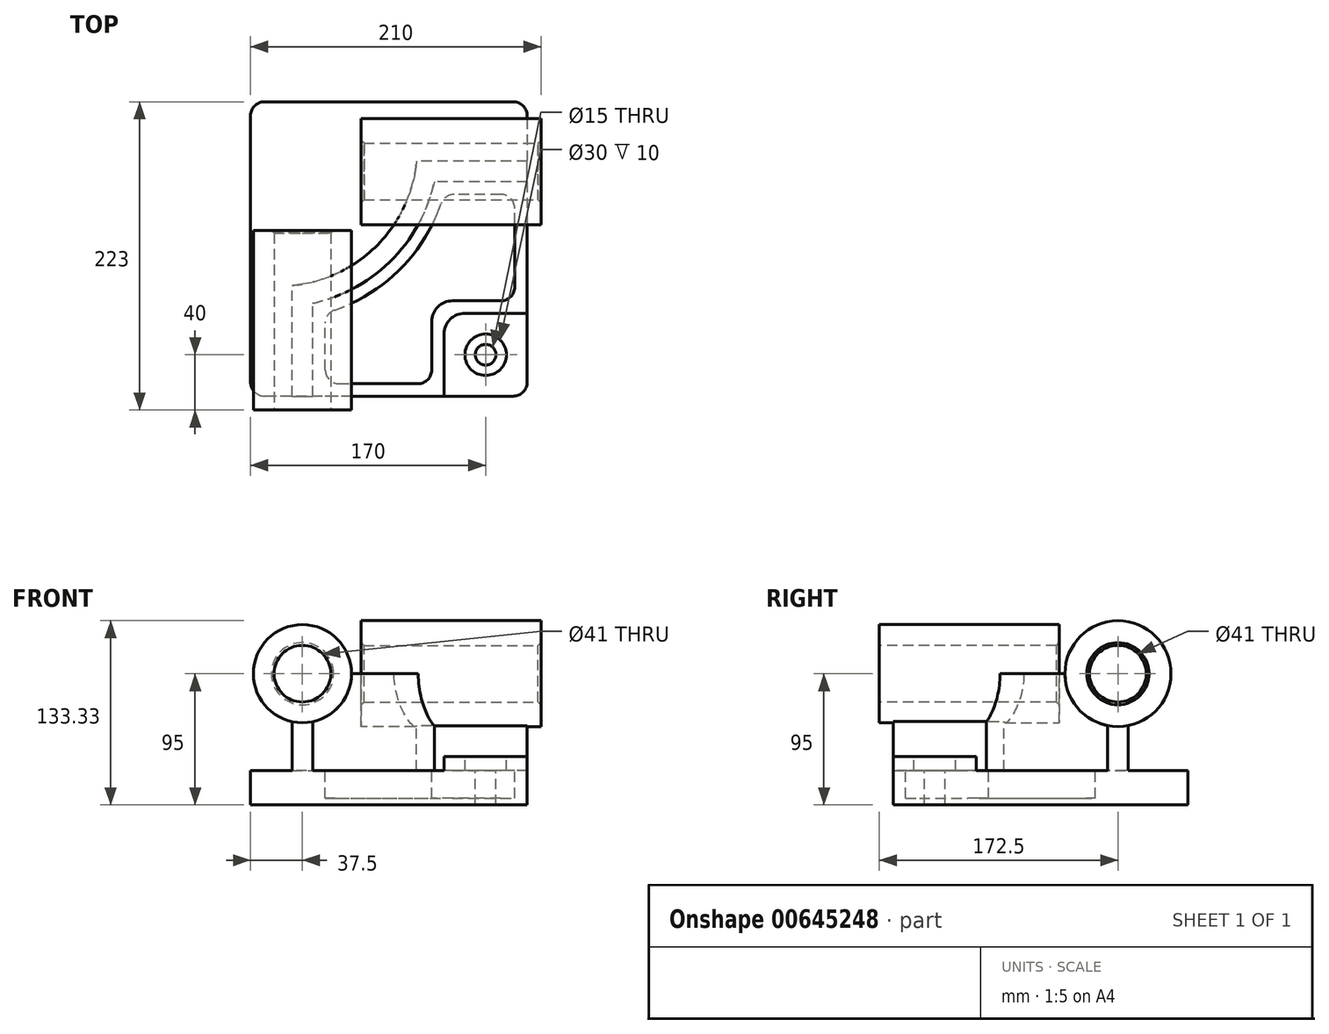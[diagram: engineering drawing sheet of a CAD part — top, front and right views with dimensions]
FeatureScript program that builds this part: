
annotation { "Feature Type Name" : "Feature", "Feature Type Description" : "" }
export const myFeature = defineFeature(function(context is Context, id is Id, definition is map)
    precondition{}
    {
        {
            var Q0;
            Q0=qCreatedBy(makeId("Top.planeOp"),FACE);
            var sketch = newSketch(context, id + "F0", { "sketchPlane" : qUnion([Q0])});
            skLineSegment(sketch, "E0.bottom", {"start": v(100, 106.5) * mm, "end": v(-100, 106.5) * mm});
            skLineSegment(sketch, "E0.top", {"start": v(100, -106.5) * mm, "end": v(-100, -106.5) * mm});
            skLineSegment(sketch, "E0.left", {"start": v(100, 106.5) * mm, "end": v(100, -106.5) * mm});
            skLineSegment(sketch, "E0.right", {"start": v(-100, 106.5) * mm, "end": v(-100, -106.5) * mm});
            skPoint(sketch, "E0.middle", {"position": v(0, 0) * mm});
            skSolve(sketch);
        }
        {
            var Q0;
            Q0 = qSketchRegion(id + "F0", true);
            var Q1;
            Q1=makeQuery(id+"F0.imprint","IMPRINT",FACE,{"disambiguationData":[TD([[makeQuery(id+"F0.imprint","IMPRINT",EDGE,{"derivedFrom":sQuery(id+"F0.wireOp",EDGE,"E0.bottom")}),1.0]])]});
            extrude(context, id + "F1", {"entities" : qUnion([Q0, Q1]), "depth" : 95 * mm, "offsetDistance" : 25 * mm});
        }
        {
            var Q0;
            Q0=makeQuery(id+"F1.opExtrude","CAP_FACE",FACE,{"disambiguationData":[OSD([sQuery(id+"F0.wireOp",EDGE,"E0.bottom"),sQuery(id+"F0.wireOp",EDGE,"E0.top"),sQuery(id+"F0.wireOp",EDGE,"E0.left"),sQuery(id+"F0.wireOp",EDGE,"E0.right")])],"isStart":false});
            var sketch = newSketch(context, id + "F2", { "sketchPlane" : qUnion([Q0])});
            skLineSegment(sketch, "E1", {"start": v(-70, -106.5) * mm, "end": v(-70, -26.5) * mm});
            skLineSegment(sketch, "E2", {"start": v(100, 63.5) * mm, "end": v(20, 63.5) * mm});
            skLineSegment(sketch, "E3.bottom", {"start": v(100, -106.5) * mm, "end": v(40, -106.5) * mm});
            skLineSegment(sketch, "E3.top", {"start": v(100, -46.5) * mm, "end": v(40, -46.5) * mm});
            skLineSegment(sketch, "E3.left", {"start": v(100, -106.5) * mm, "end": v(100, -46.5) * mm});
            skLineSegment(sketch, "E3.right", {"start": v(40, -106.5) * mm, "end": v(40, -46.5) * mm});
            skPoint(sketch, "E4.positionSnap0", {"position": v(70, -106.5) * mm});
            skLineSegment(sketch, "E5", {"start": v(70, -46.5) * mm, "end": v(70, -106.5) * mm, "construction": true});
            skPoint(sketch, "E6", {"position": v(70, -76.5) * mm});
            skArc(sketch, "E7", {"start": v(-70, -26.5) * mm, "mid": v(-8.83, 2.33) * mm, "end": v(20, 63.5) * mm});
            skLineSegment(sketch, "E8.0", {"start": v(-55, -106.5) * mm, "end": v(-55, -39.3) * mm});
            skArc(sketch, "E8.1", {"start": v(-55, -39.3) * mm, "mid": v(1.77, -8.27) * mm, "end": v(32.8, 48.5) * mm});
            skLineSegment(sketch, "E8.2", {"start": v(100, 48.5) * mm, "end": v(32.8, 48.5) * mm});
            skLineSegment(sketch, "E9.0", {"start": v(-46, -97.5) * mm, "end": v(-46, -46.33) * mm});
            skArc(sketch, "E9.1", {"start": v(-46, -46.33) * mm, "mid": v(8.14, -14.64) * mm, "end": v(39.83, 39.5) * mm});
            skLineSegment(sketch, "E9.2", {"start": v(91, 39.5) * mm, "end": v(39.83, 39.5) * mm});
            skLineSegment(sketch, "E10", {"start": v(-46, -97.5) * mm, "end": v(31, -97.5) * mm});
            skLineSegment(sketch, "E11", {"start": v(31, -97.5) * mm, "end": v(31, -37.5) * mm});
            skLineSegment(sketch, "E12", {"start": v(31, -37.5) * mm, "end": v(91, -37.5) * mm});
            skLineSegment(sketch, "E13", {"start": v(91, -37.5) * mm, "end": v(91, 39.5) * mm});
            skSolve(sketch);
        }
        {
            var Q0;
            Q0=makeQuery(id+"F2.imprint","IMPRINT",FACE,{"disambiguationData":[TD([[makeQuery(id+"F2.imprint","IMPRINT",EDGE,{"derivedFrom":sQuery(id+"F2.wireOp",EDGE,"E3.bottom")}),-1.0]])]});
            extrude(context, id + "F3", {"entities" : qUnion([Q0]), "operationType" : NewBodyOperationType.REMOVE, "oppositeDirection" : true, "depth" : 60 * mm, "offsetDistance" : 25 * mm});
        }
        {
            var Q0;
            Q0=makeQuery(id+"F2.imprint","IMPRINT",FACE,{"disambiguationData":[TD([[makeQuery(id+"F2.imprint","IMPRINT",EDGE,{"derivedFrom":sQuery(id+"F2.wireOp",EDGE,"E9.0")}),-1.0]])]});
            extrude(context, id + "F4", {"entities" : qUnion([Q0]), "operationType" : NewBodyOperationType.REMOVE, "oppositeDirection" : true, "depth" : 90 * mm, "offsetDistance" : 25 * mm});
        }
        {
            var Q0;
            {var subQ1=sQuery(id+"F2.wireOp",EDGE,"E3.top");Q0=makeQuery(id+"F2.imprint","IMPRINT",FACE,{"disambiguationData":[TD([[makeQuery(id+"F2.imprint","IMPRINT",EDGE,{"derivedFrom":subQ1}),-1.0]])]});}
            extrude(context, id + "F5", {"entities" : qUnion([Q0]), "operationType" : NewBodyOperationType.REMOVE, "oppositeDirection" : true, "depth" : 70 * mm, "offsetDistance" : 25 * mm});
        }
        {
            var Q0;
            {var subQ2=sQuery(id+"F2.wireOp",EDGE,"E1");Q0=makeQuery(id+"F2.imprint","IMPRINT",FACE,{"disambiguationData":[TD([[makeQuery(id+"F2.imprint","IMPRINT",EDGE,{"derivedFrom":subQ2}),1.0]])]});}
            extrude(context, id + "F6", {"entities" : qUnion([Q0]), "operationType" : NewBodyOperationType.REMOVE, "oppositeDirection" : true, "depth" : 70 * mm, "offsetDistance" : 25 * mm});
        }
        {
            var Q0;
            Q0=makeQuery(id+"F1.opExtrude","SWEPT_FACE",FACE,{"disambiguationData":[OSD([sQuery(id+"F0.wireOp",EDGE,"E0.top")])]});
            var sketch = newSketch(context, id + "F7", { "sketchPlane" : qUnion([Q0])});
            skPoint(sketch, "E14", {"position": v(-62.5, 95) * mm});
            skCircle(sketch, "E15", {"center": v(-62.5, 95) * mm, "radius": 35.5 * mm});
            skCircle(sketch, "E16", {"center": v(-62.5, 95) * mm, "radius": 20.5 * mm});
            skSolve(sketch);
        }
        {
            var Q0;
            Q0=makeQuery(id+"F1.opExtrude","SWEPT_FACE",FACE,{"disambiguationData":[OSD([sQuery(id+"F0.wireOp",EDGE,"E0.left")])]});
            var sketch = newSketch(context, id + "F8", { "sketchPlane" : qUnion([Q0])});
            skPoint(sketch, "E17", {"position": v(56, 95) * mm});
            skCircle(sketch, "E18", {"center": v(56, 95) * mm, "radius": 38.33 * mm});
            skCircle(sketch, "E19", {"center": v(56, 95) * mm, "radius": 20.5 * mm});
            skSolve(sketch);
        }
        {
            var Q0;
            {var subQ1=sQuery(id+"F0.wireOp",EDGE,"E0.top");var subQ6=makeQuery(id+"F1.opExtrude","CAP_EDGE",EDGE,{"disambiguationData":[OSD([subQ1])],"isStart":false});Q0=makeQuery(id+"F7.imprint","IMPRINT",FACE,{"disambiguationData":[TD([[makeQuery(id+"F7.imprint","IMPRINT",EDGE,{"derivedFrom":subQ6}),-1.0]])]});}
            var Q1;
            {var subQ1=sQuery(id+"F0.wireOp",EDGE,"E0.top");var subQ6=makeQuery(id+"F1.opExtrude","CAP_EDGE",EDGE,{"disambiguationData":[OSD([subQ1])],"isStart":false});Q1=makeQuery(id+"F7.imprint","IMPRINT",FACE,{"disambiguationData":[TD([[makeQuery(id+"F7.imprint","IMPRINT",EDGE,{"derivedFrom":subQ6}),1.0]])]});}
            var Q2;
            {var subQ0=sQuery(id+"F7.wireOp",EDGE,"E15");var subQ1=sQuery(id+"F0.wireOp",EDGE,"E0.top");var subQ2=makeQuery(id+"F5.boolean.opBoolean","COPY",EDGE,{"derivedFrom":makeQuery(id+"F5.opExtrude","SWEPT_EDGE",EDGE,{"disambiguationData":[OSD([subQ1,sQuery(id+"F2.wireOp",EDGE,"E8.0")])]})});var subQ3=makeQuery(id+"F7.imprint","INTERSECT",VERTEX,{"derivedFrom":[subQ2,subQ0]});Q2=makeQuery(id+"F7.imprint","IMPRINT",FACE,{"disambiguationData":[TD([[makeQuery(id+"F7.imprint","IMPRINT",EDGE,{"disambiguationData":[TD([[subQ3,-1.0]])],"derivedFrom":subQ0}),1.0]])]});}
            var Q3;
            {var subQ0=sQuery(id+"F7.wireOp",EDGE,"E15");var subQ1=sQuery(id+"F0.wireOp",EDGE,"E0.top");var subQ2=makeQuery(id+"F5.boolean.opBoolean","COPY",EDGE,{"derivedFrom":makeQuery(id+"F5.opExtrude","SWEPT_EDGE",EDGE,{"disambiguationData":[OSD([subQ1,sQuery(id+"F2.wireOp",EDGE,"E8.0")])]})});var subQ3=makeQuery(id+"F7.imprint","INTERSECT",VERTEX,{"derivedFrom":[subQ2,subQ0]});Q3=makeQuery(id+"F7.imprint","IMPRINT",FACE,{"disambiguationData":[TD([[makeQuery(id+"F7.imprint","IMPRINT",EDGE,{"disambiguationData":[TD([[subQ3,1.0]])],"derivedFrom":subQ0}),1.0]])]});}
            extrude(context, id + "F9", {"entities" : qUnion([Q0, Q1, Q2, Q3]), "operationType" : NewBodyOperationType.ADD, "depth" : 10 * mm, "offsetDistance" : 25 * mm, "hasSecondDirection" : true, "secondDirectionOppositeDirection" : true, "secondDirectionDepth" : 120 * mm});
        }
        {
            var Q0;
            Q0=makeQuery(id+"F9.opExtrude","CAP_FACE",FACE,{"disambiguationData":[OSD([sQuery(id+"F7.wireOp",EDGE,"E15")])],"isStart":false});
            var sketch = newSketch(context, id + "F10", { "sketchPlane" : qUnion([Q0])});
            skCircle(sketch, "E20", {"center": v(-62.5, 95) * mm, "radius": 20.5 * mm});
            skSolve(sketch);
        }
        {
            var Q0;
            Q0=makeQuery(id+"F10.imprint","IMPRINT",FACE,{"disambiguationData":[TD([[makeQuery(id+"F10.imprint","IMPRINT",EDGE,{"derivedFrom":sQuery(id+"F10.wireOp",EDGE,"E20")}),1.0]])]});
            extrude(context, id + "F11", {"entities" : qUnion([Q0]), "operationType" : NewBodyOperationType.REMOVE, "endBound" : BoundingType.THROUGH_ALL, "oppositeDirection" : true, "depth" : 25 * mm, "offsetDistance" : 25 * mm});
        }
        {
            var Q0;
            {var subQ1=sQuery(id+"F0.wireOp",EDGE,"E0.left");var subQ6=makeQuery(id+"F1.opExtrude","CAP_EDGE",EDGE,{"disambiguationData":[OSD([subQ1])],"isStart":false});Q0=makeQuery(id+"F8.imprint","IMPRINT",FACE,{"disambiguationData":[TD([[makeQuery(id+"F8.imprint","IMPRINT",EDGE,{"derivedFrom":subQ6}),-1.0]])]});}
            var Q1;
            {var subQ0=sQuery(id+"F8.wireOp",EDGE,"E18");var subQ1=sQuery(id+"F0.wireOp",EDGE,"E0.left");var subQ2=makeQuery(id+"F5.boolean.opBoolean","COPY",EDGE,{"derivedFrom":makeQuery(id+"F5.opExtrude","SWEPT_EDGE",EDGE,{"disambiguationData":[OSD([subQ1,sQuery(id+"F2.wireOp",EDGE,"E8.2")])]})});var subQ3=makeQuery(id+"F8.imprint","INTERSECT",VERTEX,{"derivedFrom":[subQ2,subQ0]});Q1=makeQuery(id+"F8.imprint","IMPRINT",FACE,{"disambiguationData":[TD([[makeQuery(id+"F8.imprint","IMPRINT",EDGE,{"disambiguationData":[TD([[subQ3,1.0]])],"derivedFrom":subQ0}),1.0]])]});}
            var Q2;
            {var subQ1=sQuery(id+"F0.wireOp",EDGE,"E0.left");var subQ6=makeQuery(id+"F1.opExtrude","CAP_EDGE",EDGE,{"disambiguationData":[OSD([subQ1])],"isStart":false});Q2=makeQuery(id+"F8.imprint","IMPRINT",FACE,{"disambiguationData":[TD([[makeQuery(id+"F8.imprint","IMPRINT",EDGE,{"derivedFrom":subQ6}),1.0]])]});}
            var Q3;
            {var subQ0=sQuery(id+"F8.wireOp",EDGE,"E18");var subQ1=sQuery(id+"F0.wireOp",EDGE,"E0.left");var subQ2=makeQuery(id+"F5.boolean.opBoolean","COPY",EDGE,{"derivedFrom":makeQuery(id+"F5.opExtrude","SWEPT_EDGE",EDGE,{"disambiguationData":[OSD([subQ1,sQuery(id+"F2.wireOp",EDGE,"E8.2")])]})});var subQ3=makeQuery(id+"F8.imprint","INTERSECT",VERTEX,{"derivedFrom":[subQ2,subQ0]});Q3=makeQuery(id+"F8.imprint","IMPRINT",FACE,{"disambiguationData":[TD([[makeQuery(id+"F8.imprint","IMPRINT",EDGE,{"disambiguationData":[TD([[subQ3,-1.0]])],"derivedFrom":subQ0}),1.0]])]});}
            extrude(context, id + "F12", {"entities" : qUnion([Q0, Q1, Q2, Q3]), "operationType" : NewBodyOperationType.ADD, "depth" : 10 * mm, "offsetDistance" : 25 * mm, "hasSecondDirection" : true, "secondDirectionOppositeDirection" : true, "secondDirectionDepth" : 120 * mm});
        }
        {
            var Q0;
            {var subQ1=sQuery(id+"F0.wireOp",EDGE,"E0.left");var subQ6=makeQuery(id+"F1.opExtrude","CAP_EDGE",EDGE,{"disambiguationData":[OSD([subQ1])],"isStart":false});Q0=makeQuery(id+"F8.imprint","IMPRINT",FACE,{"disambiguationData":[TD([[makeQuery(id+"F8.imprint","IMPRINT",EDGE,{"derivedFrom":subQ6}),-1.0]])]});}
            var Q1;
            {var subQ1=sQuery(id+"F0.wireOp",EDGE,"E0.left");var subQ6=makeQuery(id+"F1.opExtrude","CAP_EDGE",EDGE,{"disambiguationData":[OSD([subQ1])],"isStart":false});Q1=makeQuery(id+"F8.imprint","IMPRINT",FACE,{"disambiguationData":[TD([[makeQuery(id+"F8.imprint","IMPRINT",EDGE,{"derivedFrom":subQ6}),1.0]])]});}
            extrude(context, id + "F13", {"entities" : qUnion([Q0, Q1]), "operationType" : NewBodyOperationType.REMOVE, "endBound" : BoundingType.THROUGH_ALL, "oppositeDirection" : true, "depth" : 25 * mm, "offsetDistance" : 25 * mm, "hasSecondDirection" : true, "secondDirectionBound" : SecondDirectionBoundingType.THROUGH_ALL, "secondDirectionOppositeDirection" : false, "secondDirectionDepth" : 25 * mm});
        }
        {
            var Q0;
            Q0=makeQuery(id+"F3.boolean.opBoolean","COPY",FACE,{"derivedFrom":makeQuery(id+"F3.opExtrude","CAP_FACE",FACE,{"disambiguationData":[OSD([sQuery(id+"F2.wireOp",EDGE,"E3.bottom"),sQuery(id+"F2.wireOp",EDGE,"E3.top"),sQuery(id+"F2.wireOp",EDGE,"E3.left"),sQuery(id+"F2.wireOp",EDGE,"E3.right")])],"isStart":false})});
            var sketch = newSketch(context, id + "F14", { "sketchPlane" : qUnion([Q0])});
            skPoint(sketch, "E21", {"position": v(70, -76.5) * mm});
            skPoint(sketch, "E21.positionSnap0", {"position": v(70, -46.5) * mm});
            skSolve(sketch);
        }
        {
            var Q0;
            Q0=sQuery(id+"F14.wireOp",VERTEX,"E21");
            var Q1;
            Q1=makeQuery(id+"F1.opExtrude","SWEPT_BODY",BODY,{"disambiguationData":[OSD([sQuery(id+"F0.wireOp",EDGE,"E0.bottom"),sQuery(id+"F0.wireOp",EDGE,"E0.top"),sQuery(id+"F0.wireOp",EDGE,"E0.left"),sQuery(id+"F0.wireOp",EDGE,"E0.right")])]});
            hole(context, id + "F15", {"style" : HoleStyle.C_BORE, "endStyle" : HoleEndStyle.THROUGH, "holeDiameter" : 15 * mm, "cBoreDiameter" : 30 * mm, "cBoreDepth" : 10 * mm, "majorDiameter" : 6.35 * mm, "isTappedThrough" : true, "tappedDepth" : 12 * mm, "tapClearance" : 3, "startFromSketch" : true, "locations" : qUnion([Q0]), "scope" : qUnion([Q1])});
        }
        {
            var Q0;
            Q0=makeQuery(id+"F1.opExtrude","SWEPT_EDGE",EDGE,{"disambiguationData":[OSD([sQuery(id+"F0.wireOp",EDGE,"E0.bottom"),sQuery(id+"F0.wireOp",EDGE,"E0.right")])]});
            var Q1;
            Q1=makeQuery(id+"F1.opExtrude","SWEPT_EDGE",EDGE,{"disambiguationData":[OSD([sQuery(id+"F0.wireOp",EDGE,"E0.bottom"),sQuery(id+"F0.wireOp",EDGE,"E0.left")])]});
            var Q2;
            Q2=makeQuery(id+"F1.opExtrude","SWEPT_EDGE",EDGE,{"disambiguationData":[OSD([sQuery(id+"F0.wireOp",EDGE,"E0.top"),sQuery(id+"F0.wireOp",EDGE,"E0.left")])]});
            var Q3;
            Q3=makeQuery(id+"F1.opExtrude","SWEPT_EDGE",EDGE,{"disambiguationData":[OSD([sQuery(id+"F0.wireOp",EDGE,"E0.top"),sQuery(id+"F0.wireOp",EDGE,"E0.right")])]});
            fillet(context, id + "F16", {"entities" : qUnion([Q0, Q1, Q2, Q3]), "radius" : 10 * mm, "tangentPropagation" : true, "allowEdgeOverflow" : false});
        }
        {
            var Q0;
            Q0=makeQuery(id+"F4.boolean.opBoolean","COPY",EDGE,{"derivedFrom":makeQuery(id+"F4.opExtrude","SWEPT_EDGE",EDGE,{"disambiguationData":[OSD([sQuery(id+"F2.wireOp",EDGE,"E9.1"),sQuery(id+"F2.wireOp",EDGE,"E9.2")])]})});
            var Q1;
            Q1=makeQuery(id+"F4.boolean.opBoolean","COPY",EDGE,{"derivedFrom":makeQuery(id+"F4.opExtrude","SWEPT_EDGE",EDGE,{"disambiguationData":[OSD([sQuery(id+"F2.wireOp",EDGE,"E9.2"),sQuery(id+"F2.wireOp",EDGE,"E13")])]})});
            var Q2;
            Q2=makeQuery(id+"F4.boolean.opBoolean","COPY",EDGE,{"derivedFrom":makeQuery(id+"F4.opExtrude","SWEPT_EDGE",EDGE,{"disambiguationData":[OSD([sQuery(id+"F2.wireOp",EDGE,"E12"),sQuery(id+"F2.wireOp",EDGE,"E13")])]})});
            var Q3;
            Q3=makeQuery(id+"F4.boolean.opBoolean","COPY",EDGE,{"derivedFrom":makeQuery(id+"F4.opExtrude","SWEPT_EDGE",EDGE,{"disambiguationData":[OSD([sQuery(id+"F2.wireOp",EDGE,"E9.0"),sQuery(id+"F2.wireOp",EDGE,"E9.1")])]})});
            var Q4;
            Q4=makeQuery(id+"F4.boolean.opBoolean","COPY",EDGE,{"derivedFrom":makeQuery(id+"F4.opExtrude","SWEPT_EDGE",EDGE,{"disambiguationData":[OSD([sQuery(id+"F2.wireOp",EDGE,"E9.0"),sQuery(id+"F2.wireOp",EDGE,"E10")])]})});
            var Q5;
            Q5=makeQuery(id+"F4.boolean.opBoolean","COPY",EDGE,{"derivedFrom":makeQuery(id+"F4.opExtrude","SWEPT_EDGE",EDGE,{"disambiguationData":[OSD([sQuery(id+"F2.wireOp",EDGE,"E10"),sQuery(id+"F2.wireOp",EDGE,"E11")])]})});
            fillet(context, id + "F17", {"entities" : qUnion([Q0, Q1, Q2, Q3, Q4, Q5]), "radius" : 10 * mm, "tangentPropagation" : true, "allowEdgeOverflow" : false});
        }
        {
            var Q0;
            Q0=makeQuery(id+"F4.boolean.opBoolean","COPY",EDGE,{"derivedFrom":makeQuery(id+"F4.opExtrude","SWEPT_EDGE",EDGE,{"disambiguationData":[OSD([sQuery(id+"F2.wireOp",EDGE,"E11"),sQuery(id+"F2.wireOp",EDGE,"E12")])]})});
            var Q1;
            Q1=makeQuery(id+"F5.boolean.opBoolean","COPY",EDGE,{"derivedFrom":makeQuery(id+"F5.opExtrude","SWEPT_EDGE",EDGE,{"disambiguationData":[OSD([sQuery(id+"F2.wireOp",EDGE,"E3.top"),sQuery(id+"F2.wireOp",EDGE,"E3.right")])]})});
            fillet(context, id + "F18", {"entities" : qUnion([Q0, Q1]), "radius" : 15 * mm, "tangentPropagation" : true, "allowEdgeOverflow" : false});
        }
        {
            var Q0;
            Q0=makeQuery(id+"F11.boolean.opBoolean","COPY",EDGE,{"derivedFrom":makeQuery(id+"F11.opExtrude","CAP_EDGE",EDGE,{"disambiguationData":[OSD([sQuery(id+"F10.wireOp",EDGE,"E20")])],"isStart":true})});
            var Q1;
            Q1=makeQuery(id+"F11.boolean.opBoolean","INTERSECT",EDGE,{"derivedFrom":[makeQuery(id+"F9.opExtrude","CAP_FACE",FACE,{"disambiguationData":[OSD([sQuery(id+"F7.wireOp",EDGE,"E15")])],"isStart":true}),makeQuery(id+"F11.opExtrude","SWEPT_FACE",FACE,{"disambiguationData":[OSD([sQuery(id+"F10.wireOp",EDGE,"E20")])]})]});
            var Q2;
            Q2=makeQuery(id+"F13.boolean.opBoolean","INTERSECT",EDGE,{"derivedFrom":[makeQuery(id+"F12.opExtrude","CAP_FACE",FACE,{"disambiguationData":[OSD([sQuery(id+"F8.wireOp",EDGE,"E18")])],"isStart":true}),makeQuery(id+"F13.opExtrude","SWEPT_FACE",FACE,{"disambiguationData":[OSD([sQuery(id+"F8.wireOp",EDGE,"E19")])]})]});
            var Q3;
            Q3=makeQuery(id+"F13.boolean.opBoolean","INTERSECT",EDGE,{"derivedFrom":[makeQuery(id+"F12.opExtrude","CAP_FACE",FACE,{"disambiguationData":[OSD([sQuery(id+"F8.wireOp",EDGE,"E18")])],"isStart":false}),makeQuery(id+"F13.opExtrude","SWEPT_FACE",FACE,{"disambiguationData":[OSD([sQuery(id+"F8.wireOp",EDGE,"E19")])]})]});
            chamfer(context, id + "F19", {"entities" : qUnion([Q0, Q1, Q2, Q3]), "width" : 2 * mm, "tangentPropagation" : true});
        }
    });
